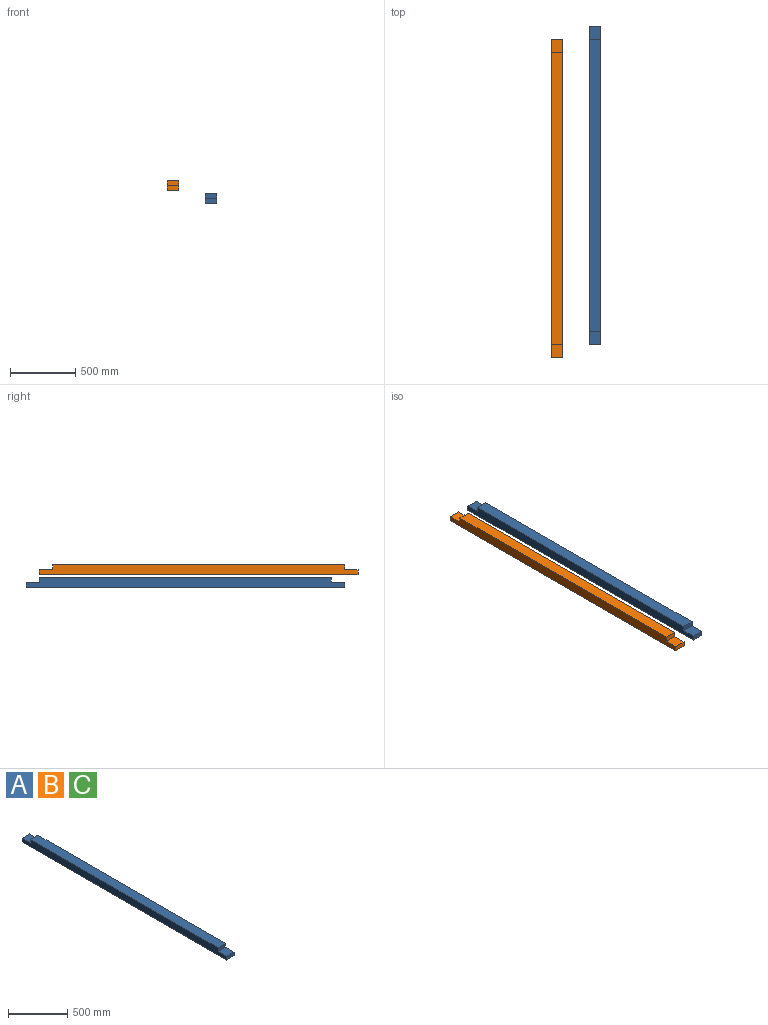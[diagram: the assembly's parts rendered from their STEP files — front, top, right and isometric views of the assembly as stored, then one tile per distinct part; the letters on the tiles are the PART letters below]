
ASSEMBLY  parts=3 mates=1
PART A: 10 faces, bbox 88.9x2438.4x76.2 mm
  f0: plane 101.6x88.9mm, normal (0,0,1), area 9032.2mm2, adj f1,f3,f6,f9
  f1: plane 2438.4x76.2mm, normal (1,0,0), area 178064.2mm2, adj f0,f2,f4,f5,f6,f7,f8,f9
  f2: plane 101.6x88.9mm, normal (0,0,1), area 9032.2mm2, adj f1,f3,f5,f8
  f3: plane 2438.4x76.2mm, normal (-1,0,0), area 178064.2mm2, adj f0,f2,f4,f5,f6,f7,f8,f9
  f4: plane 2438.4x88.9mm, normal (0,0,-1), area 216773.8mm2, adj f1,f3,f5,f6
  f5: plane 88.9x38.1mm, normal (0,-1,0), area 3387.1mm2, adj f1,f2,f3,f4
  f6: plane 88.9x38.1mm, normal (0,1,0), area 3387.1mm2, adj f0,f1,f3,f4
  f7: plane 2235.2x88.9mm, normal (0,0,1), area 198709.3mm2, adj f1,f3,f8,f9
  f8: plane 88.9x38.1mm, normal (0,-1,0), area 3387.1mm2, adj f1,f2,f3,f7
  f9: plane 88.9x38.1mm, normal (0,1,0), area 3387.1mm2, adj f0,f1,f3,f7
PART B: same geometry as A
PART C: same geometry as A
PLACE A t=(2.67,2.02,0.72)mm
PLACE B t=(-288.55,-100.96,98.45)mm
PLACE C t=(2.67,2.02,0.72)mm
MATE fastened A.f0 <-> C.f0  axis (0,0,1) through (2.67,1170.42,19.77)mm
